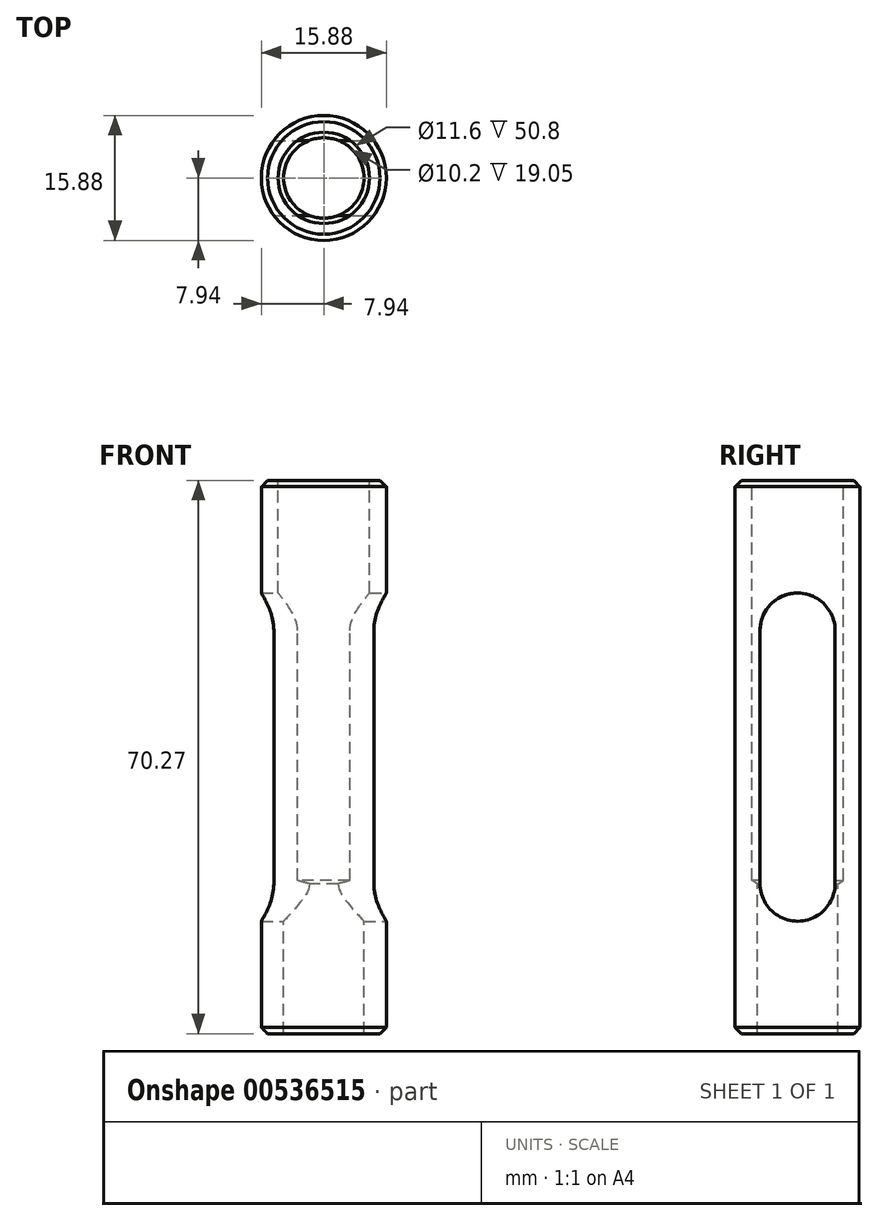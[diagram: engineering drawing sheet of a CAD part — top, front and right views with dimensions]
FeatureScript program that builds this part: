
annotation { "Feature Type Name" : "Feature", "Feature Type Description" : "" }
export const myFeature = defineFeature(function(context is Context, id is Id, definition is map)
    precondition{}
    {
        {
            var Q0;
            Q0=qCreatedBy(makeId("Front.planeOp"),FACE);
            var sketch = newSketch(context, id + "F0", { "sketchPlane" : qUnion([Q0])});
            skLineSegment(sketch, "E0", {"start": v(0, 18.41) * mm, "end": v(0, -24.55) * mm, "construction": true});
            skLineSegment(sketch, "E1", {"start": v(5.8, 0) * mm, "end": v(7.94, 0) * mm});
            skLineSegment(sketch, "E2", {"start": v(7.94, 0) * mm, "end": v(7.94, -70.27) * mm});
            skLineSegment(sketch, "E3", {"start": v(7.94, -70.27) * mm, "end": v(5.1, -70.27) * mm});
            skLineSegment(sketch, "E4", {"start": v(5.1, -70.27) * mm, "end": v(5.1, -51.22) * mm});
            skLineSegment(sketch, "E5", {"start": v(5.1, -51.22) * mm, "end": v(5.8, -50.8) * mm});
            skLineSegment(sketch, "E6", {"start": v(5.8, -50.8) * mm, "end": v(5.8, 0) * mm});
            skSolve(sketch);
        }
        {
            var Q0;
            Q0=makeQuery(id+"F0.imprint","IMPRINT",FACE,{"disambiguationData":[TD([[makeQuery(id+"F0.imprint","IMPRINT",EDGE,{"derivedFrom":sQuery(id+"F0.wireOp",EDGE,"E1")}),-1.0]])]});
            var Q1;
            Q1=sQuery(id+"F0.wireOp",EDGE,"E0");
            revolve(context, id + "F1", {"entities" : qUnion([Q0]), "axis" : qUnion([Q1]), "revolveType" : RevolveType.FULL});
        }
        {
            var Q0;
            Q0=makeQuery(id+"F1.opRevolve","SWEPT_EDGE",EDGE,{"disambiguationData":[OSD([sQuery(id+"F0.wireOp",EDGE,"E1"),sQuery(id+"F0.wireOp",EDGE,"E2")])]});
            var Q1;
            Q1=makeQuery(id+"F1.opRevolve","SWEPT_EDGE",EDGE,{"disambiguationData":[OSD([sQuery(id+"F0.wireOp",EDGE,"E2"),sQuery(id+"F0.wireOp",EDGE,"E3")])]});
            chamfer(context, id + "F2", {"entities" : qUnion([Q0, Q1]), "width" : 0.8 * mm, "tangentPropagation" : true});
        }
        {
            var Q0;
            Q0=qCreatedBy(makeId("Right.planeOp"),FACE);
            var sketch = newSketch(context, id + "F3", { "sketchPlane" : qUnion([Q0])});
            skLineSegment(sketch, "E7", {"start": v(4.76, -51.22) * mm, "end": v(4.76, -19.05) * mm});
            skArc(sketch, "E8", {"start": v(4.76, -19.05) * mm, "mid": v(0, -14.29) * mm, "end": v(-4.76, -19.05) * mm});
            skLineSegment(sketch, "E9", {"start": v(-4.76, -19.05) * mm, "end": v(-4.76, -51.22) * mm});
            skArc(sketch, "E10", {"start": v(-4.76, -51.22) * mm, "mid": v(0, -55.98) * mm, "end": v(4.76, -51.22) * mm});
            skSolve(sketch);
        }
        {
            var Q0;
            Q0 = qSketchRegion(id + "F3", true);
            extrude(context, id + "F4", {"entities" : qUnion([Q0]), "operationType" : NewBodyOperationType.REMOVE, "endBound" : BoundingType.SYMMETRIC, "oppositeDirection" : true, "depth" : 25.4 * mm, "offsetDistance" : 25.4 * mm});
        }
    });
